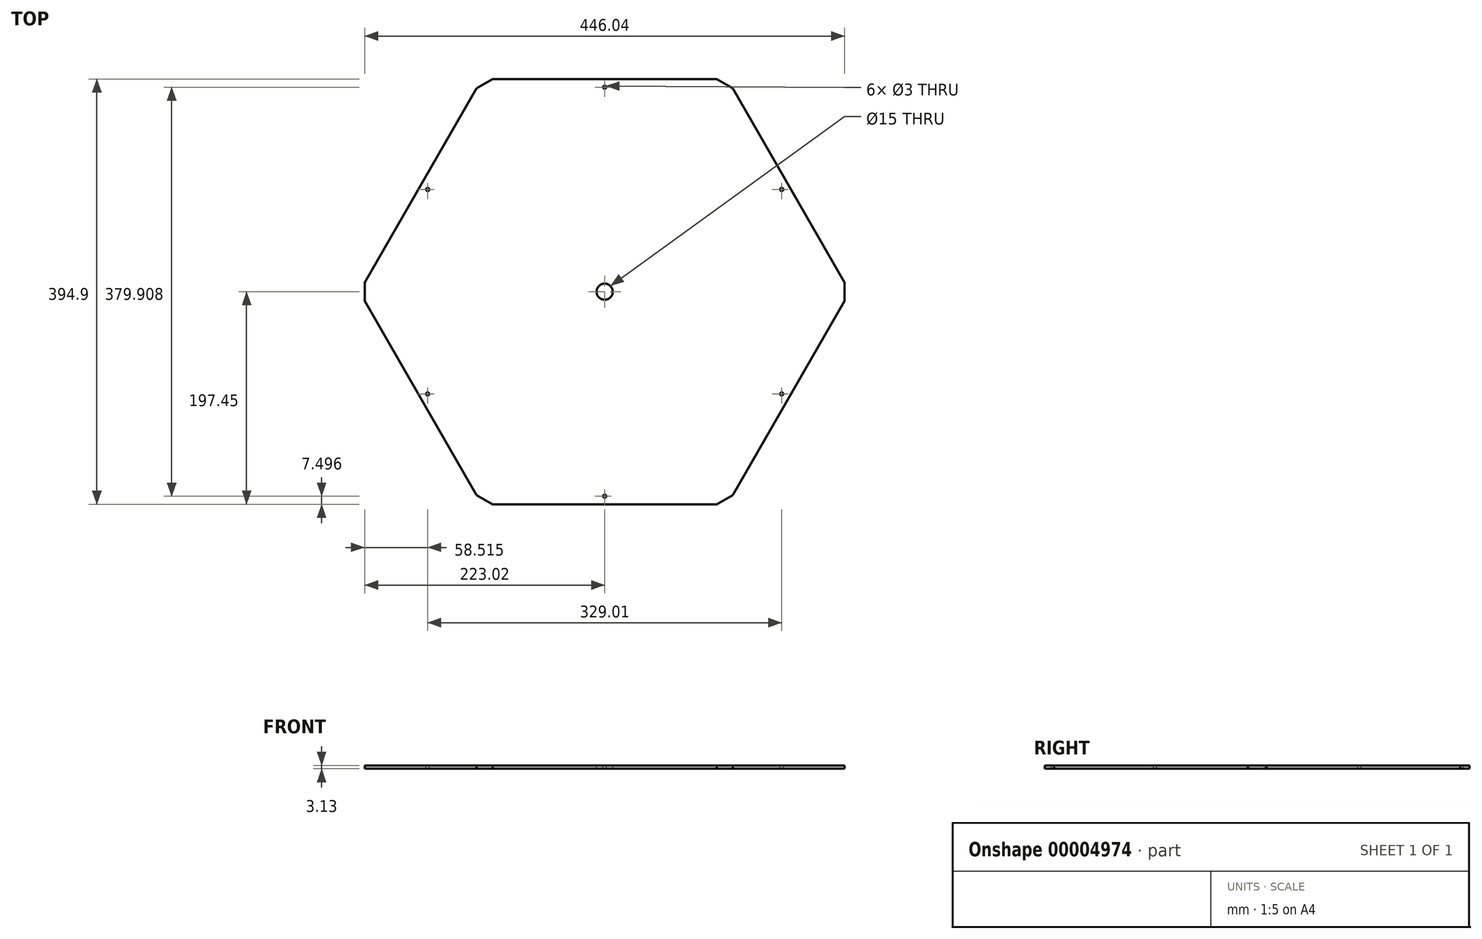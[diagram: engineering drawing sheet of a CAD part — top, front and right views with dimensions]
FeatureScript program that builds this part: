
annotation { "Feature Type Name" : "Feature", "Feature Type Description" : "" }
export const myFeature = defineFeature(function(context is Context, id is Id, definition is map)
    precondition{}
    {
        {
            var Q0;
            Q0=qCreatedBy(makeId("Top.planeOp"),FACE);
            var sketch = newSketch(context, id + "F0", { "sketchPlane" : qUnion([Q0])});
            skCircle(sketch, "E0", {"center": v(0, 0) * mm, "radius": 228 * mm, "construction": true});
            skLineSegment(sketch, "E1", {"start": v(-114, 197.45) * mm, "end": v(114, 197.45) * mm});
            skLineSegment(sketch, "E2", {"start": v(114, 197.45) * mm, "end": v(228, 0) * mm});
            skLineSegment(sketch, "E3", {"start": v(228, 0) * mm, "end": v(114, -197.45) * mm});
            skLineSegment(sketch, "E4", {"start": v(114, -197.45) * mm, "end": v(-114, -197.45) * mm});
            skLineSegment(sketch, "E5", {"start": v(-114, -197.45) * mm, "end": v(-228, 0) * mm});
            skLineSegment(sketch, "E6", {"start": v(-228, 0) * mm, "end": v(-114, 197.45) * mm});
            skSolve(sketch);
        }
        {
            var Q0;
            Q0 = qSketchRegion(id + "F0", true);
            extrude(context, id + "F1", {"entities" : qUnion([Q0]), "depth" : 3.12 * mm});
        }
        {
            var Q0;
            Q0=makeQuery(id+"F1.opExtrude","CAP_FACE",FACE,{"disambiguationData":[OSD([sQuery(id+"F0.wireOp",EDGE,"E1"),sQuery(id+"F0.wireOp",EDGE,"E2"),sQuery(id+"F0.wireOp",EDGE,"E3"),sQuery(id+"F0.wireOp",EDGE,"E4"),sQuery(id+"F0.wireOp",EDGE,"E5"),sQuery(id+"F0.wireOp",EDGE,"E6")])],"isStart":false});
            var sketch = newSketch(context, id + "F2", { "sketchPlane" : qUnion([Q0])});
            skCircle(sketch, "E7", {"center": v(0, 0) * mm, "radius": 7.5 * mm});
            skLineSegment(sketch, "E8", {"start": v(-118.98, 188.83) * mm, "end": v(-104.04, 197.45) * mm});
            skLineSegment(sketch, "E9", {"start": v(-104.04, 197.45) * mm, "end": v(-114, 197.45) * mm});
            skLineSegment(sketch, "E10", {"start": v(-114, 197.45) * mm, "end": v(-118.98, 188.83) * mm});
            skLineSegment(sketch, "E11.1.0", {"start": v(-228, 0) * mm, "end": v(-223.02, -8.63) * mm});
            skLineSegment(sketch, "E11.1.1", {"start": v(-223.02, 8.63) * mm, "end": v(-228, 0) * mm});
            skLineSegment(sketch, "E11.1.2", {"start": v(-223.02, -8.63) * mm, "end": v(-223.02, 8.62) * mm});
            skLineSegment(sketch, "E11.2.0", {"start": v(-114, -197.45) * mm, "end": v(-104.04, -197.45) * mm});
            skLineSegment(sketch, "E11.2.1", {"start": v(-118.98, -188.83) * mm, "end": v(-114, -197.45) * mm});
            skLineSegment(sketch, "E11.2.2", {"start": v(-104.04, -197.45) * mm, "end": v(-118.98, -188.83) * mm});
            skLineSegment(sketch, "E11.3.0", {"start": v(114, -197.45) * mm, "end": v(118.98, -188.83) * mm});
            skLineSegment(sketch, "E11.3.1", {"start": v(104.04, -197.45) * mm, "end": v(114, -197.45) * mm});
            skLineSegment(sketch, "E11.3.2", {"start": v(118.98, -188.83) * mm, "end": v(104.04, -197.45) * mm});
            skLineSegment(sketch, "E11.4.0", {"start": v(228, 0) * mm, "end": v(223.02, 8.62) * mm});
            skLineSegment(sketch, "E11.4.1", {"start": v(223.02, -8.63) * mm, "end": v(228, 0) * mm});
            skLineSegment(sketch, "E11.4.2", {"start": v(223.02, 8.62) * mm, "end": v(223.02, -8.63) * mm});
            skLineSegment(sketch, "E11.5.0", {"start": v(114, 197.45) * mm, "end": v(104.04, 197.45) * mm});
            skLineSegment(sketch, "E11.5.1", {"start": v(118.98, 188.83) * mm, "end": v(114, 197.45) * mm});
            skLineSegment(sketch, "E11.5.2", {"start": v(104.04, 197.45) * mm, "end": v(118.98, 188.83) * mm});
            skSolve(sketch);
        }
        {
            var Q0;
            Q0 = qSketchRegion(id + "F2", true);
            extrude(context, id + "F3", {"entities" : qUnion([Q0]), "operationType" : NewBodyOperationType.REMOVE, "endBound" : BoundingType.THROUGH_ALL, "oppositeDirection" : true, "depth" : 25 * mm});
        }
        {
            var Q0;
            Q0=makeQuery(id+"F1.opExtrude","CAP_FACE",FACE,{"disambiguationData":[OSD([sQuery(id+"F0.wireOp",EDGE,"E1"),sQuery(id+"F0.wireOp",EDGE,"E2"),sQuery(id+"F0.wireOp",EDGE,"E3"),sQuery(id+"F0.wireOp",EDGE,"E4"),sQuery(id+"F0.wireOp",EDGE,"E5"),sQuery(id+"F0.wireOp",EDGE,"E6")])],"isStart":false});
            var sketch = newSketch(context, id + "F4", { "sketchPlane" : qUnion([Q0])});
            skLineSegment(sketch, "E12", {"start": v(-171, 98.73) * mm, "end": v(0, 0) * mm, "construction": true});
            skCircle(sketch, "E13", {"center": v(-164.5, 94.98) * mm, "radius": 1.5 * mm});
            skCircle(sketch, "E14.1.0", {"center": v(-164.5, -94.98) * mm, "radius": 1.5 * mm});
            skCircle(sketch, "E14.2.0", {"center": v(0, -189.95) * mm, "radius": 1.5 * mm});
            skCircle(sketch, "E14.3.0", {"center": v(164.5, -94.98) * mm, "radius": 1.5 * mm});
            skCircle(sketch, "E14.4.0", {"center": v(164.5, 94.98) * mm, "radius": 1.5 * mm});
            skCircle(sketch, "E14.5.0", {"center": v(0, 189.95) * mm, "radius": 1.5 * mm});
            skPoint(sketch, "E14.center", {"position": v(0, 0) * mm});
            skSolve(sketch);
        }
        {
            var Q0;
            Q0 = qSketchRegion(id + "F4", true);
            extrude(context, id + "F5", {"entities" : qUnion([Q0]), "operationType" : NewBodyOperationType.REMOVE, "endBound" : BoundingType.THROUGH_ALL, "oppositeDirection" : true, "depth" : 25 * mm});
        }
    });
